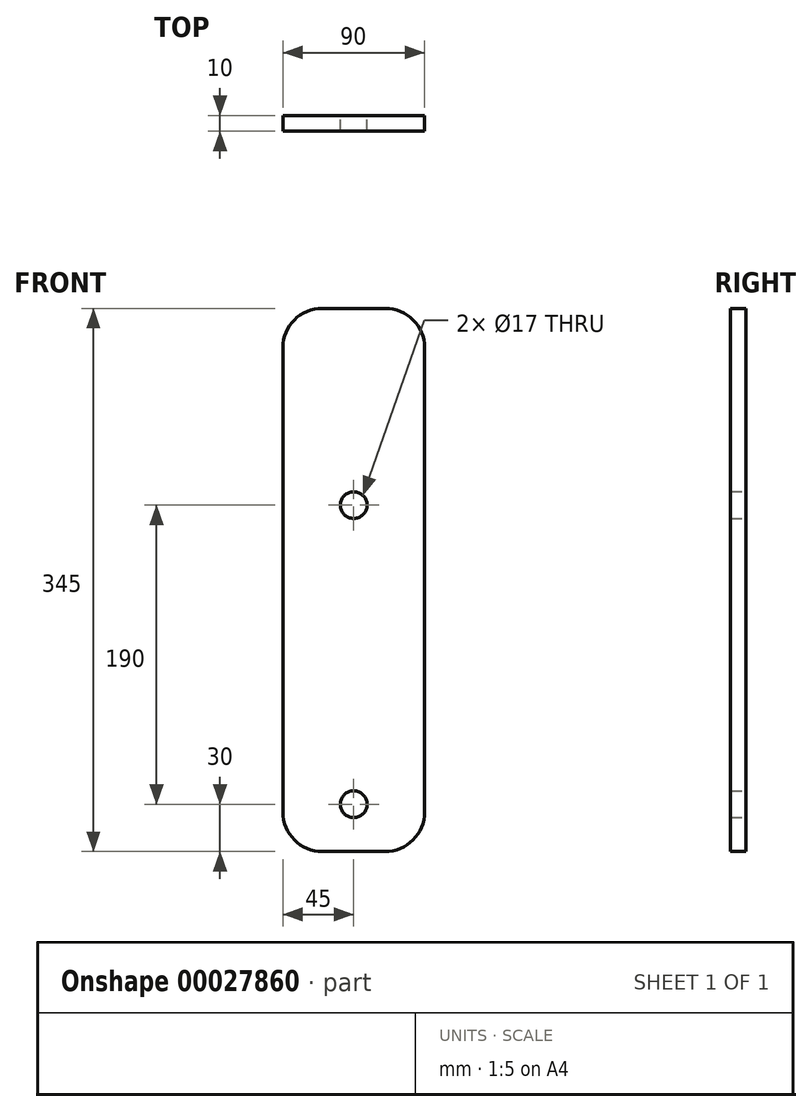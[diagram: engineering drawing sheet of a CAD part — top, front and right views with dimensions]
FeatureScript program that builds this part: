
annotation { "Feature Type Name" : "Feature", "Feature Type Description" : "" }
export const myFeature = defineFeature(function(context is Context, id is Id, definition is map)
    precondition{}
    {
        {
            var Q0;
            Q0=qCreatedBy(makeId("Front.planeOp"),FACE);
            var sketch = newSketch(context, id + "F0", { "sketchPlane" : qUnion([Q0])});
            skLineSegment(sketch, "E0.bottom", {"start": v(-25, 0) * mm, "end": v(-65, 0) * mm});
            skLineSegment(sketch, "E0.top", {"start": v(-25, -345) * mm, "end": v(-65, -345) * mm});
            skLineSegment(sketch, "E0.left", {"start": v(0, -25) * mm, "end": v(0, -320) * mm});
            skLineSegment(sketch, "E0.right", {"start": v(-90, -25) * mm, "end": v(-90, -320) * mm});
            skCircle(sketch, "E1", {"center": v(-45, -125) * mm, "radius": 8.5 * mm});
            skCircle(sketch, "E2", {"center": v(-45, -315) * mm, "radius": 8.5 * mm});
            skPoint(sketch, "E3.visualSharp", {"position": v(-90, 0) * mm});
            skArc(sketch, "E3.filletArc", {"start": v(-65, 0) * mm, "mid": v(-82.68, -7.32) * mm, "end": v(-90, -25) * mm});
            skPoint(sketch, "E4.visualSharp", {"position": v(0, 0) * mm});
            skArc(sketch, "E4.filletArc", {"start": v(0, -25) * mm, "mid": v(-7.32, -7.32) * mm, "end": v(-25, 0) * mm});
            skPoint(sketch, "E5.visualSharp", {"position": v(0, -345) * mm});
            skArc(sketch, "E5.filletArc", {"start": v(-25, -345) * mm, "mid": v(-7.32, -337.68) * mm, "end": v(0, -320) * mm});
            skPoint(sketch, "E6.visualSharp", {"position": v(-90, -345) * mm});
            skArc(sketch, "E6.filletArc", {"start": v(-90, -320) * mm, "mid": v(-82.68, -337.68) * mm, "end": v(-65, -345) * mm});
            skSolve(sketch);
        }
        {
            var Q0;
            Q0=makeQuery(id+"F0.imprint","IMPRINT",FACE,{"disambiguationData":[TD([[makeQuery(id+"F0.imprint","IMPRINT",EDGE,{"derivedFrom":sQuery(id+"F0.wireOp",EDGE,"E0.bottom")}),1.0]])]});
            extrude(context, id + "F1", {"entities" : qUnion([Q0]), "depth" : 10 * mm});
        }
    });
